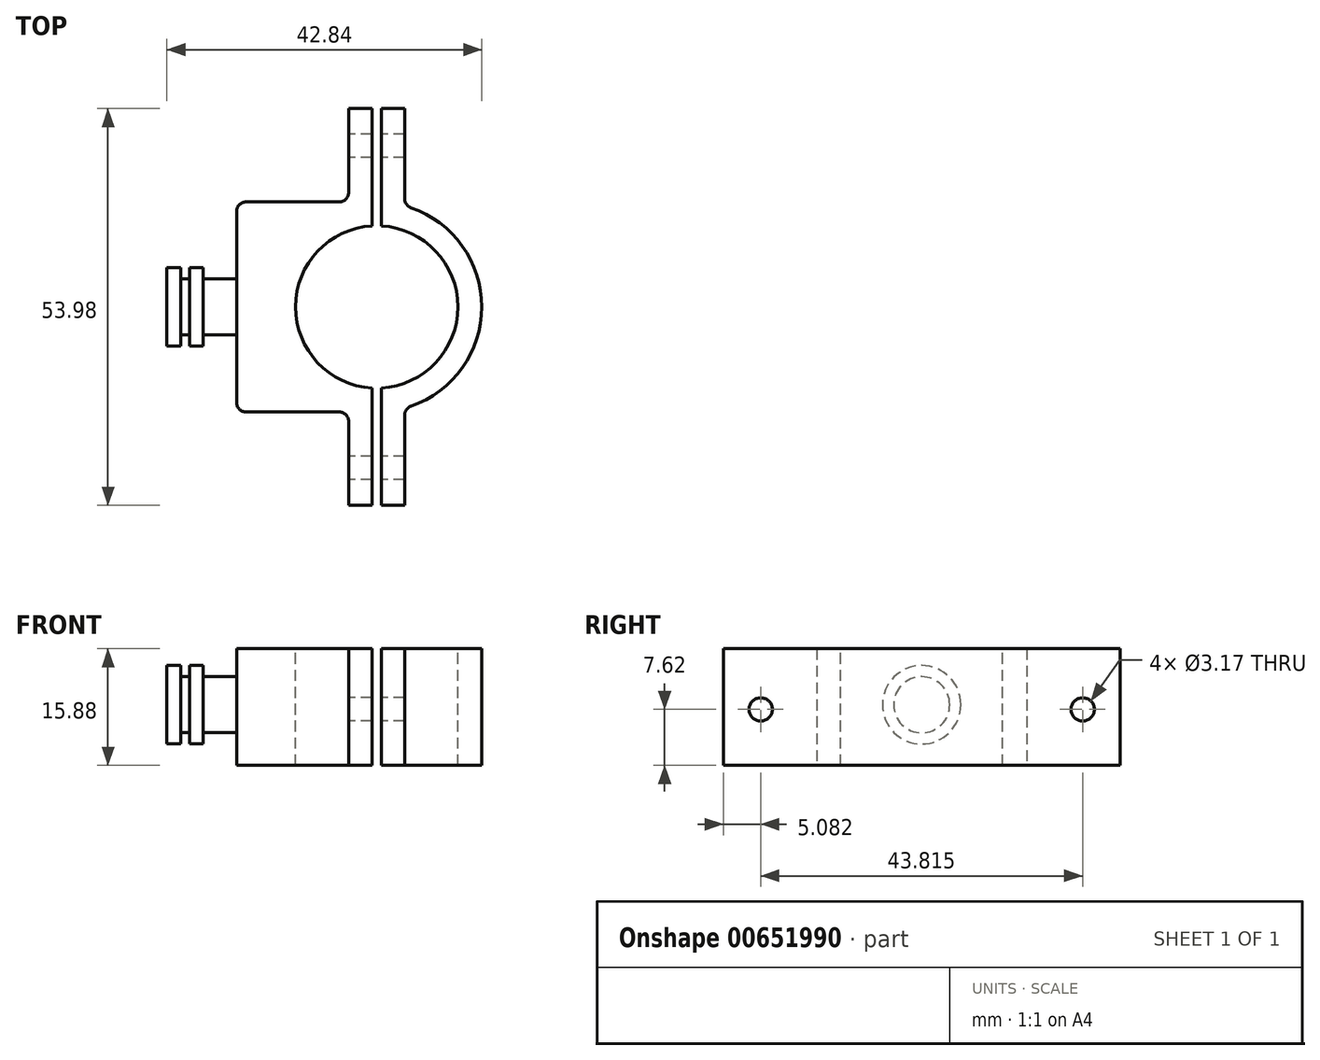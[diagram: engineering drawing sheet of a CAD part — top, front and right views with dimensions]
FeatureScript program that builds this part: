
annotation { "Feature Type Name" : "Feature", "Feature Type Description" : "" }
export const myFeature = defineFeature(function(context is Context, id is Id, definition is map)
    precondition{}
    {
        {
            var Q0;
            Q0=qCreatedBy(makeId("Top.planeOp"),FACE);
            var sketch = newSketch(context, id + "F0", { "sketchPlane" : qUnion([Q0])});
            skLineSegment(sketch, "E0", {"start": v(-5.08, 14.29) * mm, "end": v(-17.78, 14.29) * mm});
            skLineSegment(sketch, "E1", {"start": v(-19.05, 13.02) * mm, "end": v(-19.05, -13.02) * mm});
            skLineSegment(sketch, "E2", {"start": v(-17.78, -14.29) * mm, "end": v(-5.08, -14.29) * mm});
            skLineSegment(sketch, "E3", {"start": v(-3.8, 15.56) * mm, "end": v(-3.8, 26.99) * mm});
            skLineSegment(sketch, "E4", {"start": v(-3.8, 26.99) * mm, "end": v(3.81, 26.99) * mm});
            skLineSegment(sketch, "E5", {"start": v(3.81, 26.99) * mm, "end": v(3.81, 14.7) * mm});
            skLineSegment(sketch, "E6", {"start": v(3.8, -14.7) * mm, "end": v(3.8, -26.99) * mm});
            skLineSegment(sketch, "E7", {"start": v(3.8, -26.99) * mm, "end": v(-3.8, -26.99) * mm});
            skLineSegment(sketch, "E8", {"start": v(-3.8, -26.99) * mm, "end": v(-3.8, -15.56) * mm});
            skArc(sketch, "E9", {"start": v(4.67, -13.5) * mm, "mid": v(14.29, 0) * mm, "end": v(4.67, 13.5) * mm});
            skPoint(sketch, "E10.visualSharp", {"position": v(-3.8, 14.29) * mm});
            skArc(sketch, "E10.filletArc", {"start": v(-5.08, 14.29) * mm, "mid": v(-4.18, 14.66) * mm, "end": v(-3.8, 15.56) * mm});
            skPoint(sketch, "E11.visualSharp", {"position": v(-3.8, -14.29) * mm});
            skArc(sketch, "E11.filletArc", {"start": v(-3.8, -15.56) * mm, "mid": v(-4.18, -14.66) * mm, "end": v(-5.08, -14.29) * mm});
            skPoint(sketch, "E12.visualSharp", {"position": v(3.8, -13.77) * mm});
            skArc(sketch, "E12.filletArc", {"start": v(4.67, -13.5) * mm, "mid": v(4.05, -13.97) * mm, "end": v(3.8, -14.7) * mm});
            skPoint(sketch, "E13.visualSharp", {"position": v(3.8, 13.77) * mm});
            skArc(sketch, "E13.filletArc", {"start": v(3.81, 14.7) * mm, "mid": v(4.05, 13.97) * mm, "end": v(4.67, 13.5) * mm});
            skPoint(sketch, "E14.visualSharp", {"position": v(-19.05, 14.29) * mm});
            skArc(sketch, "E14.filletArc", {"start": v(-17.78, 14.29) * mm, "mid": v(-18.68, 13.92) * mm, "end": v(-19.05, 13.02) * mm});
            skPoint(sketch, "E15.visualSharp", {"position": v(-19.05, -14.29) * mm});
            skArc(sketch, "E15.filletArc", {"start": v(-19.05, -13.02) * mm, "mid": v(-18.68, -13.92) * mm, "end": v(-17.78, -14.29) * mm});
            skSolve(sketch);
        }
        {
            var Q0;
            Q0=makeQuery(id+"F0.imprint","IMPRINT",FACE,{"disambiguationData":[TD([[makeQuery(id+"F0.imprint","IMPRINT",EDGE,{"derivedFrom":sQuery(id+"F0.wireOp",EDGE,"E0")}),1.0]])]});
            extrude(context, id + "F1", {"entities" : qUnion([Q0]), "depth" : 15.88 * mm, "offsetDistance" : 25.4 * mm});
        }
        {
            var Q0;
            Q0=makeQuery(id+"F1.opExtrude","SWEPT_FACE",FACE,{"disambiguationData":[OSD([sQuery(id+"F0.wireOp",EDGE,"E1")])]});
            var sketch = newSketch(context, id + "F2", { "sketchPlane" : qUnion([Q0])});
            skCircle(sketch, "E16", {"center": v(0, 8.26) * mm, "radius": 3.81 * mm});
            skSolve(sketch);
        }
        {
            var Q0;
            Q0 = qSketchRegion(id + "F2", true);
            extrude(context, id + "F3", {"entities" : qUnion([Q0]), "operationType" : NewBodyOperationType.ADD, "depth" : 4.57 * mm, "offsetDistance" : 25.4 * mm});
        }
        {
            var Q0;
            Q0=makeQuery(id+"F3.opExtrude","CAP_FACE",FACE,{"disambiguationData":[OSD([sQuery(id+"F2.wireOp",EDGE,"E16")])],"isStart":false});
            var sketch = newSketch(context, id + "F4", { "sketchPlane" : qUnion([Q0])});
            skCircle(sketch, "E17", {"center": v(0, 8.26) * mm, "radius": 5.33 * mm});
            skSolve(sketch);
        }
        {
            var Q0;
            Q0 = qSketchRegion(id + "F4", true);
            extrude(context, id + "F5", {"entities" : qUnion([Q0]), "operationType" : NewBodyOperationType.ADD, "depth" : 1.85 * mm, "offsetDistance" : 25.4 * mm});
        }
        {
            var Q0;
            Q0=makeQuery(id+"F5.opExtrude","CAP_FACE",FACE,{"disambiguationData":[OSD([sQuery(id+"F4.wireOp",EDGE,"E17")])],"isStart":false});
            var sketch = newSketch(context, id + "F6", { "sketchPlane" : qUnion([Q0])});
            skCircle(sketch, "E18", {"center": v(0, 8.26) * mm, "radius": 3.81 * mm});
            skSolve(sketch);
        }
        {
            var Q0;
            Q0 = qSketchRegion(id + "F6", true);
            extrude(context, id + "F7", {"entities" : qUnion([Q0]), "operationType" : NewBodyOperationType.ADD, "depth" : 1.22 * mm, "offsetDistance" : 25.4 * mm});
        }
        {
            var Q0;
            Q0=makeQuery(id+"F7.opExtrude","CAP_FACE",FACE,{"disambiguationData":[OSD([sQuery(id+"F6.wireOp",EDGE,"E18")])],"isStart":false});
            var sketch = newSketch(context, id + "F8", { "sketchPlane" : qUnion([Q0])});
            skCircle(sketch, "E19", {"center": v(0, 8.26) * mm, "radius": 5.33 * mm});
            skSolve(sketch);
        }
        {
            var Q0;
            Q0 = qSketchRegion(id + "F8", true);
            extrude(context, id + "F9", {"entities" : qUnion([Q0]), "operationType" : NewBodyOperationType.ADD, "depth" : 1.85 * mm, "offsetDistance" : 25.4 * mm});
        }
        {
            var Q0;
            Q0=makeQuery(id+"F1.opExtrude","SWEPT_FACE",FACE,{"disambiguationData":[OSD([sQuery(id+"F0.wireOp",EDGE,"E3")])]});
            var sketch = newSketch(context, id + "F10", { "sketchPlane" : qUnion([Q0])});
            skCircle(sketch, "E20", {"center": v(-21.9, 7.62) * mm, "radius": 1.59 * mm});
            skSolve(sketch);
        }
        {
            var Q0;
            Q0 = qSketchRegion(id + "F10", true);
            extrude(context, id + "F11", {"entities" : qUnion([Q0]), "operationType" : NewBodyOperationType.REMOVE, "oppositeDirection" : true, "depth" : 25.4 * mm, "offsetDistance" : 25.4 * mm});
        }
        {
            var Q0;
            Q0=makeQuery(id+"F1.opExtrude","SWEPT_FACE",FACE,{"disambiguationData":[OSD([sQuery(id+"F0.wireOp",EDGE,"E8")])]});
            var sketch = newSketch(context, id + "F12", { "sketchPlane" : qUnion([Q0])});
            skCircle(sketch, "E21", {"center": v(21.9, 7.62) * mm, "radius": 1.59 * mm});
            skSolve(sketch);
        }
        {
            var Q0;
            Q0 = qSketchRegion(id + "F12", true);
            extrude(context, id + "F13", {"entities" : qUnion([Q0]), "operationType" : NewBodyOperationType.REMOVE, "oppositeDirection" : true, "depth" : 25.4 * mm, "offsetDistance" : 25.4 * mm});
        }
        {
            var Q0;
            Q0=makeQuery(id+"F1.opExtrude","CAP_FACE",FACE,{"disambiguationData":[OSD([sQuery(id+"F0.wireOp",EDGE,"E0"),sQuery(id+"F0.wireOp",EDGE,"E1"),sQuery(id+"F0.wireOp",EDGE,"E2"),sQuery(id+"F0.wireOp",EDGE,"E3"),sQuery(id+"F0.wireOp",EDGE,"E4"),sQuery(id+"F0.wireOp",EDGE,"E5"),sQuery(id+"F0.wireOp",EDGE,"E6"),sQuery(id+"F0.wireOp",EDGE,"E7"),sQuery(id+"F0.wireOp",EDGE,"E8"),sQuery(id+"F0.wireOp",EDGE,"E9"),sQuery(id+"F0.wireOp",EDGE,"E10.filletArc"),sQuery(id+"F0.wireOp",EDGE,"E11.filletArc"),sQuery(id+"F0.wireOp",EDGE,"E12.filletArc"),sQuery(id+"F0.wireOp",EDGE,"E13.filletArc"),sQuery(id+"F0.wireOp",EDGE,"E14.filletArc"),sQuery(id+"F0.wireOp",EDGE,"E15.filletArc")])],"isStart":false});
            var sketch = newSketch(context, id + "F14", { "sketchPlane" : qUnion([Q0])});
            skLineSegment(sketch, "E22", {"start": v(-0.64, 31.97) * mm, "end": v(-0.64, 11.03) * mm});
            skLineSegment(sketch, "E23", {"start": v(-0.64, -36.41) * mm, "end": v(0.64, -36.41) * mm});
            skLineSegment(sketch, "E24", {"start": v(0.64, -36.41) * mm, "end": v(0.64, -11.03) * mm});
            skLineSegment(sketch, "E25", {"start": v(0.64, 31.97) * mm, "end": v(-0.64, 31.97) * mm});
            skArc(sketch, "E26", {"start": v(-0.64, 11.03) * mm, "mid": v(-11.02, 0.73) * mm, "end": v(-2.08, -10.85) * mm});
            skArc(sketch, "E27", {"start": v(-2.08, -10.85) * mm, "mid": v(-1.36, -10.96) * mm, "end": v(-0.64, -11.03) * mm});
            skLineSegment(sketch, "E28", {"start": v(-0.64, -11.03) * mm, "end": v(-0.64, -36.41) * mm});
            skLineSegment(sketch, "E29", {"start": v(0.64, 11.03) * mm, "end": v(0.64, 31.97) * mm});
            skArc(sketch, "E30", {"start": v(0.63, -11.03) * mm, "mid": v(11.05, 0) * mm, "end": v(0.63, 11.03) * mm});
            skSolve(sketch);
        }
        {
            var Q0;
            Q0 = qSketchRegion(id + "F14", true);
            extrude(context, id + "F15", {"entities" : qUnion([Q0]), "operationType" : NewBodyOperationType.REMOVE, "oppositeDirection" : true, "depth" : 25.4 * mm, "offsetDistance" : 25.4 * mm});
        }
    });
